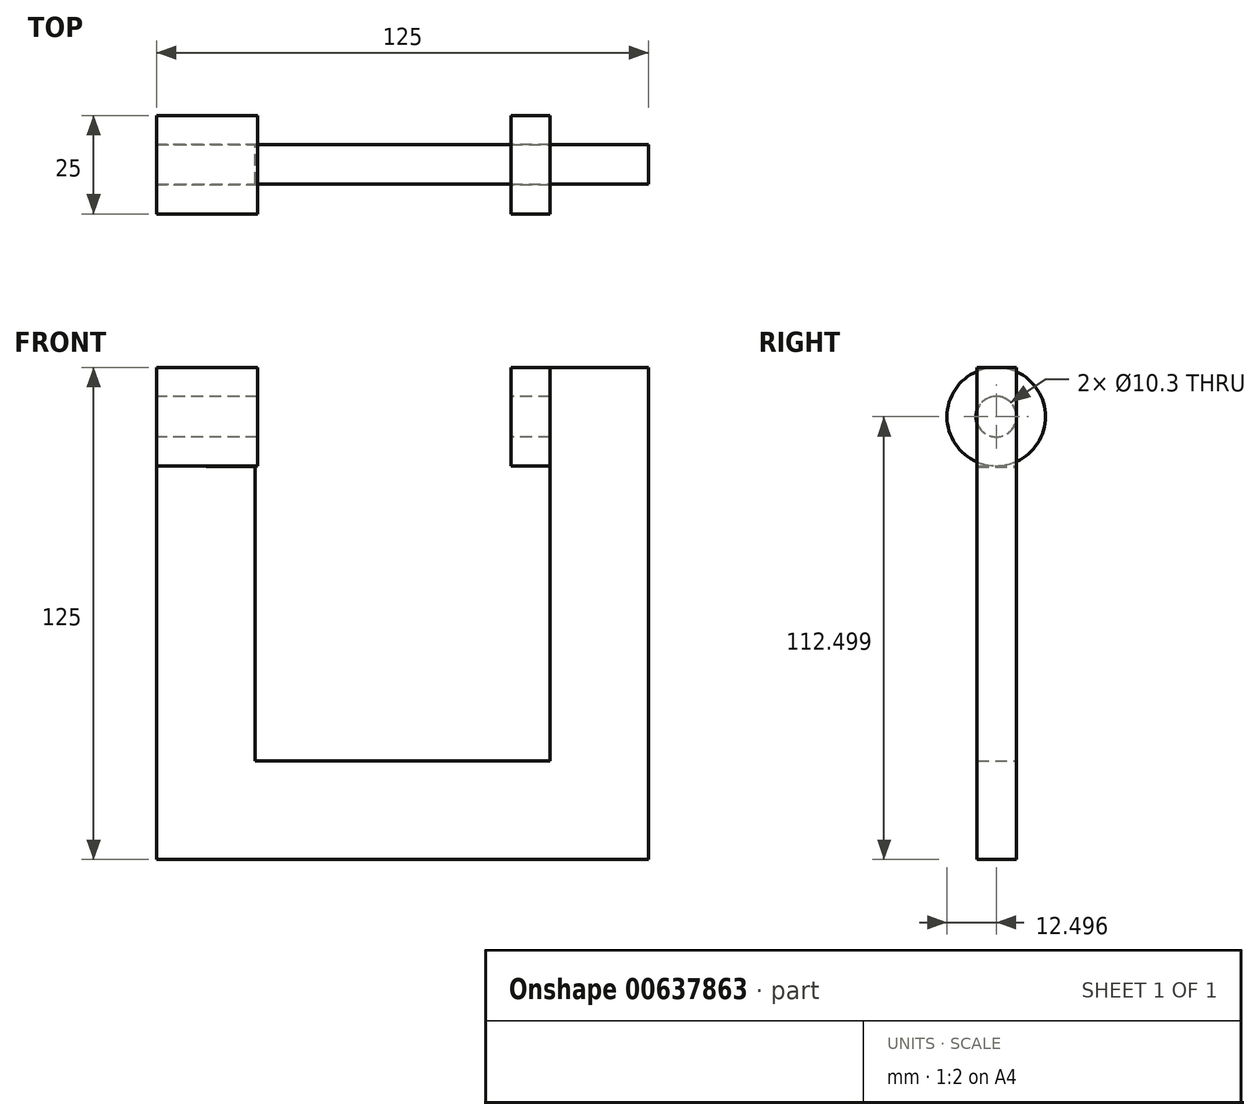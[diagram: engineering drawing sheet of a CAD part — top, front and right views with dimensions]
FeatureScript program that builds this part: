
annotation { "Feature Type Name" : "Feature", "Feature Type Description" : "" }
export const myFeature = defineFeature(function(context is Context, id is Id, definition is map)
    precondition{}
    {
        {
            var Q0;
            Q0=qCreatedBy(makeId("Front.planeOp"),FACE);
            var sketch = newSketch(context, id + "F0", { "sketchPlane" : qUnion([Q0])});
            skLineSegment(sketch, "E0", {"start": v(-60.13, 45.7) * mm, "end": v(-60.13, -54.3) * mm});
            skLineSegment(sketch, "E1", {"start": v(64.87, -54.3) * mm, "end": v(64.87, 70.7) * mm});
            skLineSegment(sketch, "E2", {"start": v(64.87, 70.7) * mm, "end": v(39.87, 70.7) * mm});
            skLineSegment(sketch, "E3", {"start": v(39.87, 70.7) * mm, "end": v(39.87, -29.3) * mm});
            skLineSegment(sketch, "E4", {"start": v(-35.13, -29.3) * mm, "end": v(-35.13, 45.42) * mm});
            skLineSegment(sketch, "E5", {"start": v(-35.13, -29.3) * mm, "end": v(39.87, -29.3) * mm});
            skLineSegment(sketch, "E6", {"start": v(-60.13, -54.3) * mm, "end": v(64.87, -54.3) * mm});
            skLineSegment(sketch, "E7", {"start": v(-60.13, 45.7) * mm, "end": v(-35.13, 45.42) * mm});
            skSolve(sketch);
        }
        {
            var Q0;
            Q0 = qSketchRegion(id + "F0", true);
            extrude(context, id + "F1", {"entities" : qUnion([Q0]), "endBound" : BoundingType.SYMMETRIC, "depth" : 10 * mm, "offsetDistance" : 25 * mm});
        }
        {
            var Q0;
            Q0=makeQuery(id+"F1.opExtrude","SWEPT_FACE",FACE,{"disambiguationData":[OSD([sQuery(id+"F0.wireOp",EDGE,"E3")])]});
            var sketch = newSketch(context, id + "F2", { "sketchPlane" : qUnion([Q0])});
            skCircle(sketch, "E8", {"center": v(0.14, 58.2) * mm, "radius": 12.5 * mm});
            skSolve(sketch);
        }
        {
            var Q0;
            Q0 = qSketchRegion(id + "F2", true);
            extrude(context, id + "F3", {"entities" : qUnion([Q0]), "depth" : 100 * mm, "offsetDistance" : 25 * mm});
        }
        {
            var Q0;
            Q0=makeQuery(id+"F1.opExtrude","CAP_FACE",FACE,{"disambiguationData":[OSD([sQuery(id+"F0.wireOp",EDGE,"E0"),sQuery(id+"F0.wireOp",EDGE,"E1"),sQuery(id+"F0.wireOp",EDGE,"E2"),sQuery(id+"F0.wireOp",EDGE,"E3"),sQuery(id+"F0.wireOp",EDGE,"E4"),sQuery(id+"F0.wireOp",EDGE,"E5"),sQuery(id+"F0.wireOp",EDGE,"E6"),sQuery(id+"F0.wireOp",EDGE,"E7")])],"isStart":false});
            var sketch = newSketch(context, id + "F4", { "sketchPlane" : qUnion([Q0])});
            skLineSegment(sketch, "E9.bottom", {"start": v(-34.5, 77.64) * mm, "end": v(29.87, 77.64) * mm});
            skLineSegment(sketch, "E9.top", {"start": v(-34.5, -1.66) * mm, "end": v(29.87, -1.66) * mm});
            skLineSegment(sketch, "E9.left", {"start": v(-34.5, 77.64) * mm, "end": v(-34.5, -1.66) * mm});
            skLineSegment(sketch, "E9.right", {"start": v(29.87, 77.64) * mm, "end": v(29.87, -1.66) * mm});
            skSolve(sketch);
        }
        {
            var Q0;
            Q0 = qSketchRegion(id + "F4", true);
            extrude(context, id + "F5", {"entities" : qUnion([Q0]), "operationType" : NewBodyOperationType.REMOVE, "oppositeDirection" : true, "depth" : 25 * mm, "offsetDistance" : 25 * mm});
        }
        {
            var Q0;
            Q0=makeQuery(id+"F5.boolean.opBoolean","COPY",FACE,{"derivedFrom":makeQuery(id+"F5.opExtrude","CAP_FACE",FACE,{"disambiguationData":[OSD([sQuery(id+"F4.wireOp",EDGE,"E9.bottom"),sQuery(id+"F4.wireOp",EDGE,"E9.top"),sQuery(id+"F4.wireOp",EDGE,"E9.left"),sQuery(id+"F4.wireOp",EDGE,"E9.right")])],"isStart":true})});
            var sketch = newSketch(context, id + "F6", { "sketchPlane" : qUnion([Q0])});
            skLineSegment(sketch, "E10.bottom", {"start": v(-29.87, 69.72) * mm, "end": v(34.4, 69.72) * mm});
            skLineSegment(sketch, "E10.top", {"start": v(-29.87, 24.32) * mm, "end": v(34.4, 24.32) * mm});
            skLineSegment(sketch, "E10.left", {"start": v(-29.87, 69.72) * mm, "end": v(-29.87, 24.32) * mm});
            skLineSegment(sketch, "E10.right", {"start": v(34.4, 69.72) * mm, "end": v(34.4, 24.32) * mm});
            skSolve(sketch);
        }
        {
            var Q0;
            Q0 = qSketchRegion(id + "F6", true);
            extrude(context, id + "F7", {"entities" : qUnion([Q0]), "operationType" : NewBodyOperationType.REMOVE, "oppositeDirection" : true, "depth" : 25 * mm, "offsetDistance" : 25 * mm});
        }
        {
            var Q0;
            Q0=makeQuery(id+"F3.opExtrude","CAP_FACE",FACE,{"disambiguationData":[OSD([sQuery(id+"F2.wireOp",EDGE,"E8")])],"isStart":false});
            var sketch = newSketch(context, id + "F8", { "sketchPlane" : qUnion([Q0])});
            skLineSegment(sketch, "E11", {"start": v(0.14, 58.2) * mm, "end": v(0.14, 45.7) * mm, "construction": true});
            skSolve(sketch);
        }
        {
            var Q0;
            Q0=sQuery(id+"F8.wireOp",VERTEX,"E11.start");
            var Q1;
            Q1=makeQuery(id+"F7.boolean.opBoolean","SPLIT",BODY,{"disambiguationData":[OD(1.0)],"derivedFrom":makeQuery(id+"F3.opExtrude","SWEPT_BODY",BODY,{"disambiguationData":[OSD([sQuery(id+"F2.wireOp",EDGE,"E8")])]})});
            hole(context, id + "F9", {"style" : HoleStyle.SIMPLE, "endStyle" : HoleEndStyle.THROUGH, "standardTappedOrClearance" : lookupTablePath({ "standard" : "ISO", "engagement" : "75%", "pitch" : "1.75 mm", "size" : "M12", "type" : "Tapped" }), "standardBlindInLast" : lookupTablePath({ "standard" : "ISO", "engagement" : "75%", "pitch" : "1.75 mm", "size" : "M12", "type" : "Tapped" }), "holeDiameter" : 10.3 * mm, "majorDiameter" : 12 * mm, "showTappedDepth" : true, "isTappedThrough" : true, "tappedDepth" : 12 * mm, "tapClearance" : 3, "locations" : qUnion([Q0]), "scope" : qUnion([Q1])});
        }
    });
